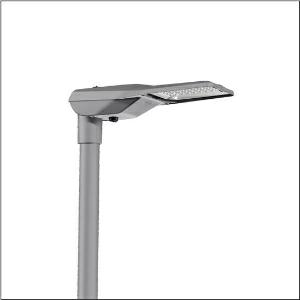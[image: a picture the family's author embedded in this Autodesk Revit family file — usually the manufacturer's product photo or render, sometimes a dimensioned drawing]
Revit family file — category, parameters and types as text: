
# Revit family: streetlight_sl_21_iq_mini___p1_0a_5xe2a31y08hb_fafd
name_source: partatom
category: Lighting Fixtures
units: mm (PartAtom-declared; Revit-internal decimal feet)

## family parameters
Cut with Voids When Loaded = No
Host = Face
Light Source = No
Part Type = Normal
Room Calculation Point = No
Round Connector Dimension = Use Diameter
Shared = No

## types (1)
- --- (1 x LED, 9750 lm, 71 W, 3000K)
    Apparent Load = 71 VA
    CIE Flux Codes = 21 50 90 100 100
    Color Rendering = 70
    Color Temperature = 3000K
    Default Elevation = 1800 mm
    Description = Streetlight SL 21 iQ mini, mast luminaire, primary light control with lens, of PMMA, primary optical cover: cover, of toughened safety glass, transparent, light distribution: P1.0a, light emission: direct distribution, primary light characteristic: asymmetric, installation type: post-top, side-entry, LED, High Power LED, rated luminous flux: 9.750lm, luminous efficacy: 137lm/W, light colour: 730, colour temperature: 3000K, control: presetting dimming logarithmic, Street-Remote, Auto-Match, Temp-Guard, Lumen-Switch, Night-Set, Smart-Wire, Light-Fading, Desk-Remote (wireless, voltage-free reading and setting of iQ features in the workshop via application-optimized NFC function/RFID function), optimised constant luminous flux control (CLO 2.0), mains connection: 220..240V, AC, 50/60Hz, start of lifetime: 71W, end of service life: 75W, reduction: 30W, luminaire housing, of diecast aluminium, powder-coated, Siteco® metallic grey (DB 702S), corrosivity category C5 mid according to DIN EN ISO 12944, please order mast flange separately, inclination adjustable: 0°, 5°, 10°, 15°, sealing non-destructively replaceable, multi-level sealing system, length: 628mm, width: 235mm, height: 110mm, mast flange for spigot size: 42mm (side-entry): 5XC10008XM4, 60/48mm (side-entry/post-top): 5XC10108XM2, 76/60mm (side-entry/post-top): 5XC10108XM1, Smart Interface below and above, protection rating (complete): IP66, insulation class (complete): insulation class II (safety insulation), certification: CE, ENEC, ENEC+, VDE, impact resistance: IK09, permissible operating ambient temperature for outdoor applications: -40..+50°C, standard-compliant lighting for roads and squares, packaging unit: 1 piece

Light Distribution: P1.0a
    Height = 110 mm
    Lamp = 1 x LED
    Lamp Light Flux = 9750 lm
    Lamp Power = 71 W
    Lamp count = 1
    Length = 625 mm
    Luminous efficacy = 137 lm/W
    Manufacturer = Siteco
    ModVariant = No
    Model = 5XE2A31Y08HB
    Number of Poles = 1
    OnlyDefault = Yes
    Power Factor = 1
    Product Name = Streetlight SL 21 iQ mini | P1.0a
    Product group = mast luminaire | pylon top
    ProductGroupID = 6100
    Protection Class = Protection class II
    Protection Degree = IP 66
    RLX_Detail_Level = 1
    RLX_Emergency_Light_Flux = 0 lm
    RLX_Emergency_Type = 0
    RLX_Emergency_Type_DB = No
    RlxData = <blob elided: 103637 chars, md5=bfa838e9>
    Socket = socket
    Standby Power = 0 W
    System Light Flux = 9750 lm
    System Power = 71 W
    Type Comments = factory setting: luminous flux: 100 % | dim-lin: 254 | 716 mA
    Type Image = l_1003514.jpg
    URL = http://relux.com
    VarID = @adj_061697
    Voltage = 0 V
    Weight = 0.00 kg
    Width = 234 mm

## geometry (parser evidence)
native form markers: Blend x4, Sweep x11
no freeform markers — native parametric forms only
